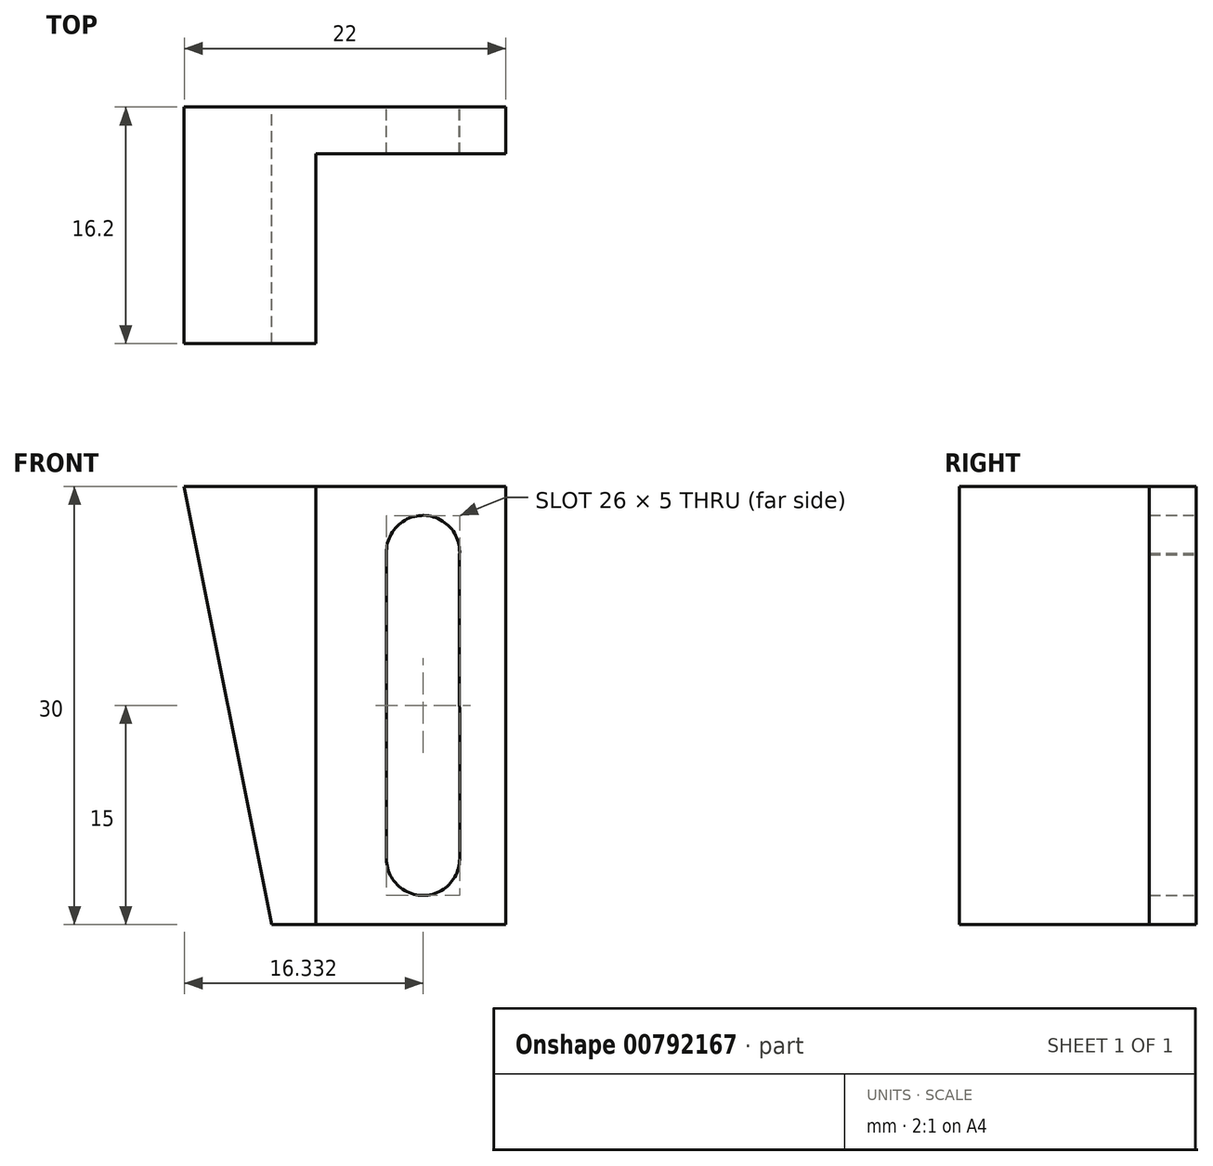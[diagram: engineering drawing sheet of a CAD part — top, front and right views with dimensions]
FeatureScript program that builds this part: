
annotation { "Feature Type Name" : "Feature", "Feature Type Description" : "" }
export const myFeature = defineFeature(function(context is Context, id is Id, definition is map)
    precondition{}
    {
        {
            var Q0;
            Q0=qCreatedBy(makeId("Front.planeOp"),FACE);
            var sketch = newSketch(context, id + "F0", { "sketchPlane" : qUnion([Q0])});
            skLineSegment(sketch, "E0", {"start": v(3.74, 0) * mm, "end": v(-9.26, 0) * mm});
            skLineSegment(sketch, "E1", {"start": v(-18.26, 30) * mm, "end": v(-9.26, 30) * mm});
            skLineSegment(sketch, "E2", {"start": v(-9.26, 30) * mm, "end": v(3.74, 30) * mm});
            skLineSegment(sketch, "E3", {"start": v(-9.26, 30) * mm, "end": v(-9.26, 0) * mm});
            skLineSegment(sketch, "E4", {"start": v(3.74, 30) * mm, "end": v(3.74, 0) * mm});
            skLineSegment(sketch, "E5", {"start": v(-9.26, 0) * mm, "end": v(-12.26, 0) * mm});
            skLineSegment(sketch, "E6", {"start": v(-12.26, 0) * mm, "end": v(-18.26, 30) * mm});
            skLineSegment(sketch, "E7", {"start": v(-9.26, 30) * mm, "end": v(-1.93, 30) * mm});
            skLineSegment(sketch, "E8", {"start": v(-1.93, 30) * mm, "end": v(-1.93, 25.5) * mm});
            skArc(sketch, "E9", {"start": v(0.57, 25.32) * mm, "mid": v(-1.88, 28) * mm, "end": v(-4.43, 25.42) * mm});
            skArc(sketch, "E10", {"start": v(-4.43, 4.5) * mm, "mid": v(-1.93, 2) * mm, "end": v(0.57, 4.5) * mm});
            skLineSegment(sketch, "E11", {"start": v(-4.43, 25.58) * mm, "end": v(-4.43, 4.5) * mm});
            skLineSegment(sketch, "E12", {"start": v(0.57, 25.68) * mm, "end": v(0.57, 4.5) * mm});
            skLineSegment(sketch, "E13.trimOffspring", {"start": v(-1.93, 4.5) * mm, "end": v(-1.93, 0) * mm});
            skSolve(sketch);
        }
        {
            var Q0;
            Q0=makeQuery(id+"F0.imprint","IMPRINT",FACE,{"disambiguationData":[TD([[makeQuery(id+"F0.imprint","IMPRINT",EDGE,{"derivedFrom":sQuery(id+"F0.wireOp",EDGE,"E1")}),-1.0]])]});
            var Q1;
            {var subQ9=sQuery(id+"F0.wireOp",EDGE,"E3");Q1=makeQuery(id+"F0.imprint","IMPRINT",FACE,{"disambiguationData":[TD([[makeQuery(id+"F0.imprint","IMPRINT",EDGE,{"derivedFrom":subQ9}),1.0]])]});}
            var Q2;
            {var subQ1=sQuery(id+"F0.wireOp",EDGE,"E2");Q2=makeQuery(id+"F0.imprint","IMPRINT",FACE,{"disambiguationData":[TD([[makeQuery(id+"F0.imprint","IMPRINT",EDGE,{"derivedFrom":subQ1}),-1.0]])]});}
            extrude(context, id + "F1", {"entities" : qUnion([Q0, Q1, Q2]), "depth" : 3.2 * mm, "offsetDistance" : 25 * mm});
        }
        {
            var Q0;
            Q0=makeQuery(id+"F1.opExtrude","CAP_FACE",FACE,{"disambiguationData":[OSD([sQuery(id+"F0.wireOp",EDGE,"E0"),sQuery(id+"F0.wireOp",EDGE,"E1"),sQuery(id+"F0.wireOp",EDGE,"E2"),sQuery(id+"F0.wireOp",EDGE,"E4"),sQuery(id+"F0.wireOp",EDGE,"E5"),sQuery(id+"F0.wireOp",EDGE,"E6"),sQuery(id+"F0.wireOp",EDGE,"E7"),sQuery(id+"F0.wireOp",EDGE,"E9"),sQuery(id+"F0.wireOp",EDGE,"E10"),sQuery(id+"F0.wireOp",EDGE,"E11"),sQuery(id+"F0.wireOp",EDGE,"E12")])],"isStart":false});
            var sketch = newSketch(context, id + "F2", { "sketchPlane" : qUnion([Q0])});
            skLineSegment(sketch, "E14", {"start": v(-18.26, 30) * mm, "end": v(-9.26, 30) * mm});
            skLineSegment(sketch, "E15", {"start": v(-9.26, 30) * mm, "end": v(-9.26, 0) * mm});
            skLineSegment(sketch, "E16", {"start": v(-9.26, 0) * mm, "end": v(-12.26, 0) * mm});
            skLineSegment(sketch, "E17", {"start": v(-12.26, 0) * mm, "end": v(-18.26, 30) * mm});
            skSolve(sketch);
        }
        {
            var Q0;
            Q0=makeQuery(id+"F2.imprint","IMPRINT",FACE,{"disambiguationData":[TD([[makeQuery(id+"F2.imprint","IMPRINT",EDGE,{"derivedFrom":sQuery(id+"F2.wireOp",EDGE,"E14")}),-1.0]])]});
            extrude(context, id + "F3", {"entities" : qUnion([Q0]), "operationType" : NewBodyOperationType.ADD, "depth" : 13 * mm, "offsetDistance" : 25 * mm});
        }
    });
